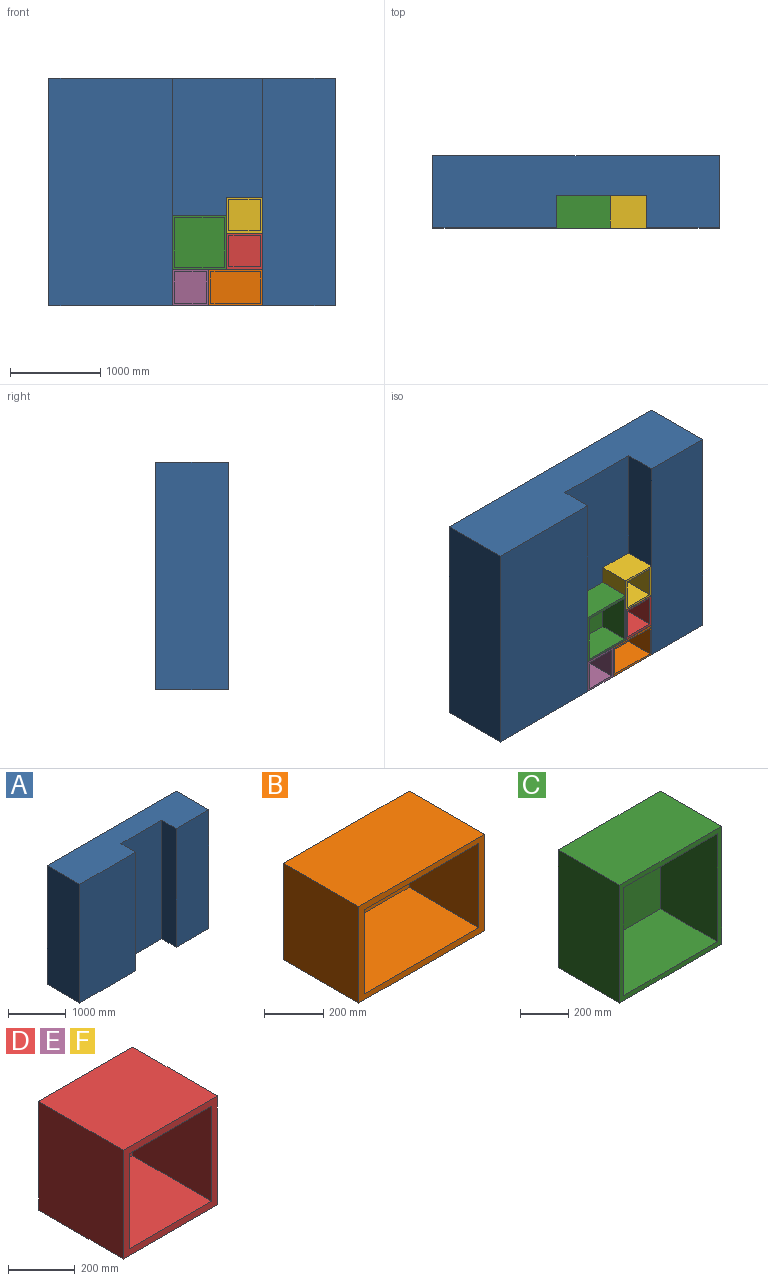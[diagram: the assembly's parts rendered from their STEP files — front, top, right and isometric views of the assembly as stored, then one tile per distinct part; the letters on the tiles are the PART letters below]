
ASSEMBLY  parts=6 mates=7
PART A: 10 faces, bbox 3170x800x2520 mm
  f0: plane 2520x1370mm, normal (0,-1,0), area 3452400mm2, adj f1,f7,f8,f9
  f1: plane 2520x360mm, normal (1,0,0), area 907200mm2, adj f0,f2,f8,f9
  f2: plane 2520x1000mm, normal (0,-1,0), area 2520000mm2, adj f1,f3,f8,f9
  f3: plane 2520x360mm, normal (-1,0,0), area 907200mm2, adj f2,f4,f8,f9
  f4: plane 2520x800mm, normal (0,-1,0), area 2016000mm2, adj f3,f5,f8,f9
  f5: plane 2520x800mm, normal (1,0,0), area 2016000mm2, adj f4,f6,f8,f9
  f6: plane 3170x2520mm, normal (0,1,0), area 7988400mm2, adj f5,f7,f8,f9
  f7: plane 2520x800mm, normal (-1,0,0), area 2016000mm2, adj f0,f6,f8,f9
  f8: plane 3170x800mm, normal (0,0,1), area 2176000mm2, adj f0,f1,f2,f3,f4,f5,f6,f7
  f9: plane 3170x800mm, normal (0,0,-1), area 2176000mm2, adj f0,f1,f2,f3,f4,f5,f6,f7
PART B: 11 faces, bbox 600x360x400 mm
  f0: plane 600x400mm, normal (0,-1,0), area 47500mm2, adj f2,f3,f4,f5,f7,f8,f9,f10
  f1: plane 600x400mm, normal (0,1,0), area 240000mm2, adj f2,f3,f4,f5
  f2: plane 400x360mm, normal (-1,0,0), area 144000mm2, adj f0,f1,f3,f4
  f3: plane 600x360mm, normal (0,0,1), area 216000mm2, adj f0,f1,f2,f5
  f4: plane 600x360mm, normal (0,0,-1), area 216000mm2, adj f0,f1,f2,f5
  f5: plane 400x360mm, normal (1,0,0), area 144000mm2, adj f0,f1,f3,f4
  f6: plane 550x350mm, normal (0,-1,0), area 192500mm2, adj f7,f8,f9,f10
  f7: plane 350x335mm, normal (1,0,0), area 117250mm2, adj f0,f6,f8,f9
  f8: plane 550x335mm, normal (0,0,-1), area 184250mm2, adj f0,f6,f7,f10
  f9: plane 550x335mm, normal (0,0,1), area 184250mm2, adj f0,f6,f7,f10
  f10: plane 350x335mm, normal (-1,0,0), area 117250mm2, adj f0,f6,f8,f9
PART C: 11 faces, bbox 600x360x600 mm
  f0: plane 600x600mm, normal (0,1,0), area 360000mm2, adj f1,f2,f3,f4
  f1: plane 600x360mm, normal (-1,0,0), area 216000mm2, adj f0,f2,f4,f5
  f2: plane 600x360mm, normal (0,0,1), area 216000mm2, adj f0,f1,f3,f5
  f3: plane 600x360mm, normal (1,0,0), area 216000mm2, adj f0,f2,f4,f5
  f4: plane 600x360mm, normal (0,0,-1), area 216000mm2, adj f0,f1,f3,f5
  f5: plane 600x600mm, normal (0,-1,0), area 57500mm2, adj f1,f2,f3,f4,f7,f8,f9,f10
  f6: plane 550x550mm, normal (0,-1,0), area 302500mm2, adj f7,f8,f9,f10
  f7: plane 550x335mm, normal (1,0,0), area 184250mm2, adj f5,f6,f8,f10
  f8: plane 550x335mm, normal (0,0,-1), area 184250mm2, adj f5,f6,f7,f9
  f9: plane 550x335mm, normal (-1,0,0), area 184250mm2, adj f5,f6,f8,f10
  f10: plane 550x335mm, normal (0,0,1), area 184250mm2, adj f5,f6,f7,f9
PART D: 11 faces, bbox 400x360x400 mm
  f0: plane 400x400mm, normal (0,1,0), area 160000mm2, adj f1,f2,f3,f4
  f1: plane 400x360mm, normal (-1,0,0), area 144000mm2, adj f0,f2,f4,f5
  f2: plane 400x360mm, normal (0,0,1), area 144000mm2, adj f0,f1,f3,f5
  f3: plane 400x360mm, normal (1,0,0), area 144000mm2, adj f0,f2,f4,f5
  f4: plane 400x360mm, normal (0,0,-1), area 144000mm2, adj f0,f1,f3,f5
  f5: plane 400x400mm, normal (0,-1,0), area 37500mm2, adj f1,f2,f3,f4,f7,f8,f9,f10
  f6: plane 350x350mm, normal (0,-1,0), area 122500mm2, adj f7,f8,f9,f10
  f7: plane 350x335mm, normal (1,0,0), area 117250mm2, adj f5,f6,f8,f10
  f8: plane 350x335mm, normal (0,0,-1), area 117250mm2, adj f5,f6,f7,f9
  f9: plane 350x335mm, normal (-1,0,0), area 117250mm2, adj f5,f6,f8,f10
  f10: plane 350x335mm, normal (0,0,1), area 117250mm2, adj f5,f6,f7,f9
PART E: same geometry as D
PART F: same geometry as D
PLACE A t=(865.83,-1495.59,2695.08)mm
PLACE B t=(865.83,-1495.59,2695.08)mm
PLACE C t=(863.53,-1495.59,2696.73)mm
PLACE D t=(1464.76,-1495.59,3099.86)mm
PLACE E t=(863.78,-1495.59,2695.82)mm
PLACE F t=(1461.56,-1495.59,3498.33)mm
MATE planar F.f0 <-> A.f2  axis (0,1,0) through (1661.56,-1495.59,3698.33)mm
MATE planar E.f0 <-> A.f2  axis (0,1,0) through (1063.78,-1495.59,2895.82)mm
MATE planar A.f2 <-> C.f0  axis (0,-1,0) through (1365.83,-1495.59,3955.08)mm
MATE planar A.f2 <-> D.f0  axis (0,-1,0) through (1365.83,-1495.59,3955.08)mm
MATE planar B.f4 <-> A.f9  axis (0,0,-1) through (1565.83,-1675.59,2695.08)mm
MATE planar B.f5 <-> A.f3  axis (1,0,0) through (1865.83,-1675.59,2895.08)mm
MATE planar B.f1 <-> A.f2  axis (0,1,0) through (1565.83,-1495.59,2895.08)mm
